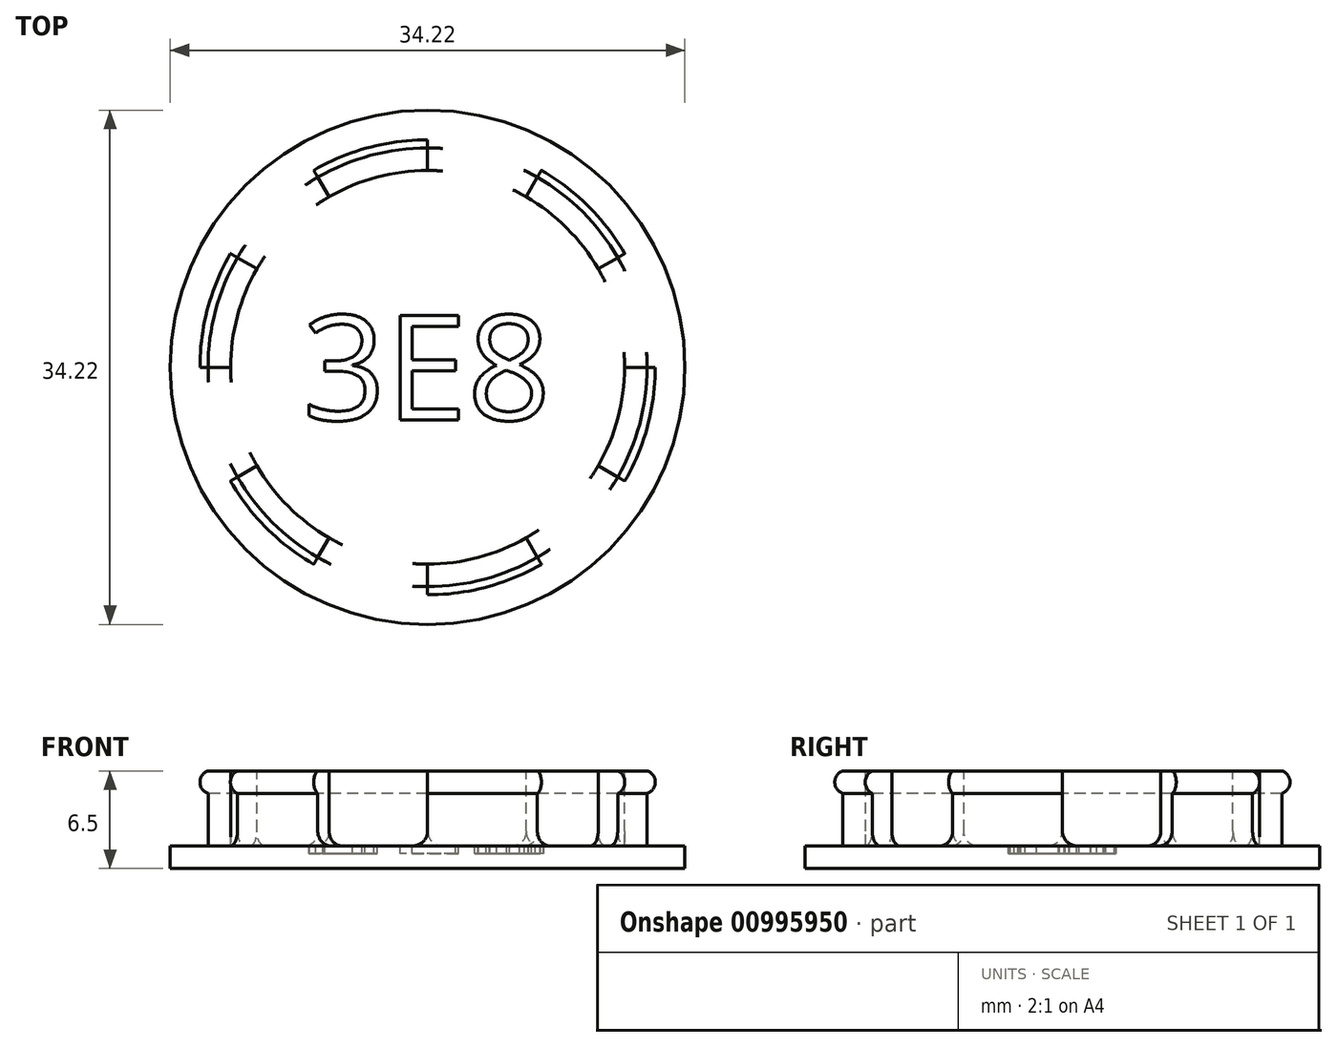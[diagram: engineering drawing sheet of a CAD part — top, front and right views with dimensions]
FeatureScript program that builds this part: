
annotation { "Feature Type Name" : "Feature", "Feature Type Description" : "" }
export const myFeature = defineFeature(function(context is Context, id is Id, definition is map)
    precondition{}
    {
        {
            var Q0;
            Q0=qCreatedBy(makeId("Front.planeOp"),FACE);
            var sketch = newSketch(context, id + "F0", { "sketchPlane" : qUnion([Q0])});
            skLineSegment(sketch, "E0", {"start": v(0, 0) * mm, "end": v(17.11, 0) * mm});
            skLineSegment(sketch, "E1", {"start": v(17.11, 0) * mm, "end": v(17.11, 1.5) * mm});
            skLineSegment(sketch, "E2", {"start": v(17.11, 1.5) * mm, "end": v(14.6, 1.5) * mm});
            skLineSegment(sketch, "E3", {"start": v(14.6, 1.5) * mm, "end": v(14.6, 5) * mm});
            skArc(sketch, "E4", {"start": v(14.6, 5) * mm, "mid": v(15.14, 5.75) * mm, "end": v(14.6, 6.5) * mm});
            skLineSegment(sketch, "E5", {"start": v(14.6, 6.5) * mm, "end": v(13.1, 6.5) * mm});
            skLineSegment(sketch, "E6", {"start": v(13.1, 6.5) * mm, "end": v(13.1, 1.5) * mm});
            skLineSegment(sketch, "E7", {"start": v(13.1, 1.5) * mm, "end": v(0, 1.5) * mm});
            skLineSegment(sketch, "E8", {"start": v(0, 1.5) * mm, "end": v(0, 0) * mm});
            skLineSegment(sketch, "E9", {"start": v(14.6, 6.5) * mm, "end": v(14.6, 5) * mm, "construction": true});
            skLineSegment(sketch, "E10", {"start": v(14.35, 5.75) * mm, "end": v(14.6, 5.75) * mm, "construction": true});
            skSolve(sketch);
        }
        {
            var Q0;
            Q0 = qSketchRegion(id + "F0", true);
            var Q1;
            Q1=sQuery(id+"F0.wireOp",EDGE,"E8");
            revolve(context, id + "F1", {"surfaceOperationType" : NewSurfaceOperationType.NEW, "entities" : qUnion([Q0]), "axis" : qUnion([Q1]), "revolveType" : RevolveType.FULL});
        }
        {
            var Q0;
            Q0=makeQuery(id+"F1.opRevolve","SWEPT_FACE",FACE,{"disambiguationData":[OSD([sQuery(id+"F0.wireOp",EDGE,"E2")])]});
            var sketch = newSketch(context, id + "F2", { "sketchPlane" : qUnion([Q0])});
            skArc(sketch, "E11", {"start": v(8.56, 14.82) * mm, "mid": v(4.43, 16.53) * mm, "end": v(0, 17.11) * mm});
            skLineSegment(sketch, "E12", {"start": v(0, 17.11) * mm, "end": v(0, 0) * mm});
            skLineSegment(sketch, "E13", {"start": v(8.56, 14.82) * mm, "end": v(0, 0) * mm});
            skLineSegment(sketch, "E14.1.0", {"start": v(-14.82, 8.56) * mm, "end": v(0, 0) * mm});
            skArc(sketch, "E14.1.1", {"start": v(-8.56, 14.82) * mm, "mid": v(-12.1, 12.1) * mm, "end": v(-14.82, 8.56) * mm});
            skLineSegment(sketch, "E14.1.2", {"start": v(-8.56, 14.82) * mm, "end": v(0, 0) * mm});
            skLineSegment(sketch, "E14.2.0", {"start": v(-14.82, -8.56) * mm, "end": v(0, 0) * mm});
            skArc(sketch, "E14.2.1", {"start": v(-17.11, 0) * mm, "mid": v(-16.53, -4.43) * mm, "end": v(-14.82, -8.56) * mm});
            skLineSegment(sketch, "E14.2.2", {"start": v(-17.11, 0) * mm, "end": v(0, 0) * mm});
            skLineSegment(sketch, "E14.3.0", {"start": v(0, -17.11) * mm, "end": v(0, 0) * mm});
            skArc(sketch, "E14.3.1", {"start": v(-8.56, -14.82) * mm, "mid": v(-4.43, -16.53) * mm, "end": v(0, -17.11) * mm});
            skLineSegment(sketch, "E14.3.2", {"start": v(-8.56, -14.82) * mm, "end": v(0, 0) * mm});
            skLineSegment(sketch, "E14.4.0", {"start": v(14.82, -8.56) * mm, "end": v(0, 0) * mm});
            skArc(sketch, "E14.4.1", {"start": v(8.56, -14.82) * mm, "mid": v(12.1, -12.1) * mm, "end": v(14.82, -8.56) * mm});
            skLineSegment(sketch, "E14.4.2", {"start": v(8.56, -14.82) * mm, "end": v(0, 0) * mm});
            skLineSegment(sketch, "E14.5.0", {"start": v(14.82, 8.56) * mm, "end": v(0, 0) * mm});
            skArc(sketch, "E14.5.1", {"start": v(17.11, 0) * mm, "mid": v(16.53, 4.43) * mm, "end": v(14.82, 8.56) * mm});
            skLineSegment(sketch, "E14.5.2", {"start": v(17.11, 0) * mm, "end": v(0, 0) * mm});
            skSolve(sketch);
        }
        {
            var Q0;
            Q0 = qSketchRegion(id + "F2", true);
            extrude(context, id + "F3", {"entities" : qUnion([Q0]), "operationType" : NewBodyOperationType.REMOVE, "endBound" : BoundingType.THROUGH_ALL, "depth" : 25 * mm, "offsetDistance" : 25 * mm});
        }
        {
            var Q0;
            Q0=makeQuery(id+"F3.boolean.opBoolean","MERGE",FACE,{"derivedFrom":[makeQuery(id+"F1.opRevolve","SWEPT_FACE",FACE,{"disambiguationData":[OSD([sQuery(id+"F0.wireOp",EDGE,"E2")])]}),makeQuery(id+"F1.opRevolve","SWEPT_FACE",FACE,{"disambiguationData":[OSD([sQuery(id+"F0.wireOp",EDGE,"E7")])]})],"fromTools":[makeQuery(id+"F3.opExtrude","CAP_FACE",FACE,{"disambiguationData":[OSD([sQuery(id+"F2.wireOp",EDGE,"E11"),sQuery(id+"F2.wireOp",EDGE,"E12"),sQuery(id+"F2.wireOp",EDGE,"E13")])],"isStart":true}),makeQuery(id+"F3.opExtrude","CAP_FACE",FACE,{"disambiguationData":[OSD([sQuery(id+"F2.wireOp",EDGE,"E14.1.0"),sQuery(id+"F2.wireOp",EDGE,"E14.1.1"),sQuery(id+"F2.wireOp",EDGE,"E14.1.2")])],"isStart":true}),makeQuery(id+"F3.opExtrude","CAP_FACE",FACE,{"disambiguationData":[OSD([sQuery(id+"F2.wireOp",EDGE,"E14.2.0"),sQuery(id+"F2.wireOp",EDGE,"E14.2.1"),sQuery(id+"F2.wireOp",EDGE,"E14.2.2")])],"isStart":true}),makeQuery(id+"F3.opExtrude","CAP_FACE",FACE,{"disambiguationData":[OSD([sQuery(id+"F2.wireOp",EDGE,"E14.3.0"),sQuery(id+"F2.wireOp",EDGE,"E14.3.1"),sQuery(id+"F2.wireOp",EDGE,"E14.3.2")])],"isStart":true}),makeQuery(id+"F3.opExtrude","CAP_FACE",FACE,{"disambiguationData":[OSD([sQuery(id+"F2.wireOp",EDGE,"E14.4.0"),sQuery(id+"F2.wireOp",EDGE,"E14.4.1"),sQuery(id+"F2.wireOp",EDGE,"E14.4.2")])],"isStart":true}),makeQuery(id+"F3.opExtrude","CAP_FACE",FACE,{"disambiguationData":[OSD([sQuery(id+"F2.wireOp",EDGE,"E14.5.0"),sQuery(id+"F2.wireOp",EDGE,"E14.5.1"),sQuery(id+"F2.wireOp",EDGE,"E14.5.2")])],"isStart":true})]});
            var sketch = newSketch(context, id + "F4", { "sketchPlane" : qUnion([Q0])});
            skText(sketch, "E15", { "text": "3E8", "fontName": "OpenSans-Regular.ttf"});
            const initialGuessF4  = {"E15": [-0.00833, -0.0035, 1, 0, 0.007]};
            skSetInitialGuess(sketch, initialGuessF4);
            skSolve(sketch);
        }
        {
            var Q0;
            Q0 = qSketchRegion(id + "F4", true);
            extrude(context, id + "F5", {"entities" : qUnion([Q0]), "operationType" : NewBodyOperationType.REMOVE, "oppositeDirection" : true, "depth" : .5 * mm, "offsetDistance" : 25 * mm});
        }
        {
            var Q0;
            Q0=makeQuery(id+"F3.boolean.opBoolean","COPY",EDGE,{"derivedFrom":makeQuery(id+"F3.opExtrude","CAP_EDGE",EDGE,{"disambiguationData":[OSD([sQuery(id+"F2.wireOp",EDGE,"E14.1.2")])],"isStart":true})});
            var Q1;
            Q1=makeQuery(id+"F3.boolean.opBoolean","COPY",EDGE,{"derivedFrom":makeQuery(id+"F3.opExtrude","CAP_EDGE",EDGE,{"disambiguationData":[OSD([sQuery(id+"F2.wireOp",EDGE,"E14.5.0")])],"isStart":true})});
            var Q2;
            Q2=makeQuery(id+"F3.boolean.opBoolean","COPY",EDGE,{"derivedFrom":makeQuery(id+"F3.opExtrude","CAP_EDGE",EDGE,{"disambiguationData":[OSD([sQuery(id+"F2.wireOp",EDGE,"E14.4.0")])],"isStart":true})});
            var Q3;
            Q3=makeQuery(id+"F3.boolean.opBoolean","COPY",EDGE,{"derivedFrom":makeQuery(id+"F3.opExtrude","CAP_EDGE",EDGE,{"disambiguationData":[OSD([sQuery(id+"F2.wireOp",EDGE,"E14.4.2")])],"isStart":true})});
            var Q4;
            Q4=makeQuery(id+"F3.boolean.opBoolean","COPY",EDGE,{"derivedFrom":makeQuery(id+"F3.opExtrude","CAP_EDGE",EDGE,{"disambiguationData":[OSD([sQuery(id+"F2.wireOp",EDGE,"E14.3.2")])],"isStart":true})});
            var Q5;
            Q5=makeQuery(id+"F3.boolean.opBoolean","COPY",EDGE,{"derivedFrom":makeQuery(id+"F3.opExtrude","CAP_EDGE",EDGE,{"disambiguationData":[OSD([sQuery(id+"F2.wireOp",EDGE,"E14.2.2")])],"isStart":true})});
            var Q6;
            Q6=makeQuery(id+"F3.boolean.opBoolean","COPY",EDGE,{"derivedFrom":makeQuery(id+"F3.opExtrude","CAP_EDGE",EDGE,{"disambiguationData":[OSD([sQuery(id+"F2.wireOp",EDGE,"E14.1.0")])],"isStart":true})});
            var Q7;
            Q7=makeQuery(id+"F3.boolean.opBoolean","COPY",EDGE,{"derivedFrom":makeQuery(id+"F3.opExtrude","CAP_EDGE",EDGE,{"disambiguationData":[OSD([sQuery(id+"F2.wireOp",EDGE,"E12")])],"isStart":true})});
            var Q8;
            Q8=makeQuery(id+"F3.boolean.opBoolean","COPY",EDGE,{"derivedFrom":makeQuery(id+"F3.opExtrude","CAP_EDGE",EDGE,{"disambiguationData":[OSD([sQuery(id+"F2.wireOp",EDGE,"E13")])],"isStart":true})});
            var Q9;
            Q9=makeQuery(id+"F3.boolean.opBoolean","COPY",EDGE,{"derivedFrom":makeQuery(id+"F3.opExtrude","CAP_EDGE",EDGE,{"disambiguationData":[OSD([sQuery(id+"F2.wireOp",EDGE,"E14.5.2")])],"isStart":true})});
            var Q10;
            Q10=makeQuery(id+"F3.boolean.opBoolean","COPY",EDGE,{"derivedFrom":makeQuery(id+"F3.opExtrude","CAP_EDGE",EDGE,{"disambiguationData":[OSD([sQuery(id+"F2.wireOp",EDGE,"E14.3.0")])],"isStart":true})});
            var Q11;
            Q11=makeQuery(id+"F3.boolean.opBoolean","COPY",EDGE,{"derivedFrom":makeQuery(id+"F3.opExtrude","CAP_EDGE",EDGE,{"disambiguationData":[OSD([sQuery(id+"F2.wireOp",EDGE,"E14.2.0")])],"isStart":true})});
            fillet(context, id + "F6", {"entities" : qUnion([Q0, Q1, Q2, Q3, Q4, Q5, Q6, Q7, Q8, Q9, Q10, Q11]), "radius" : 1 * mm, "tangentPropagation" : true, "allowEdgeOverflow" : false});
        }
    });
